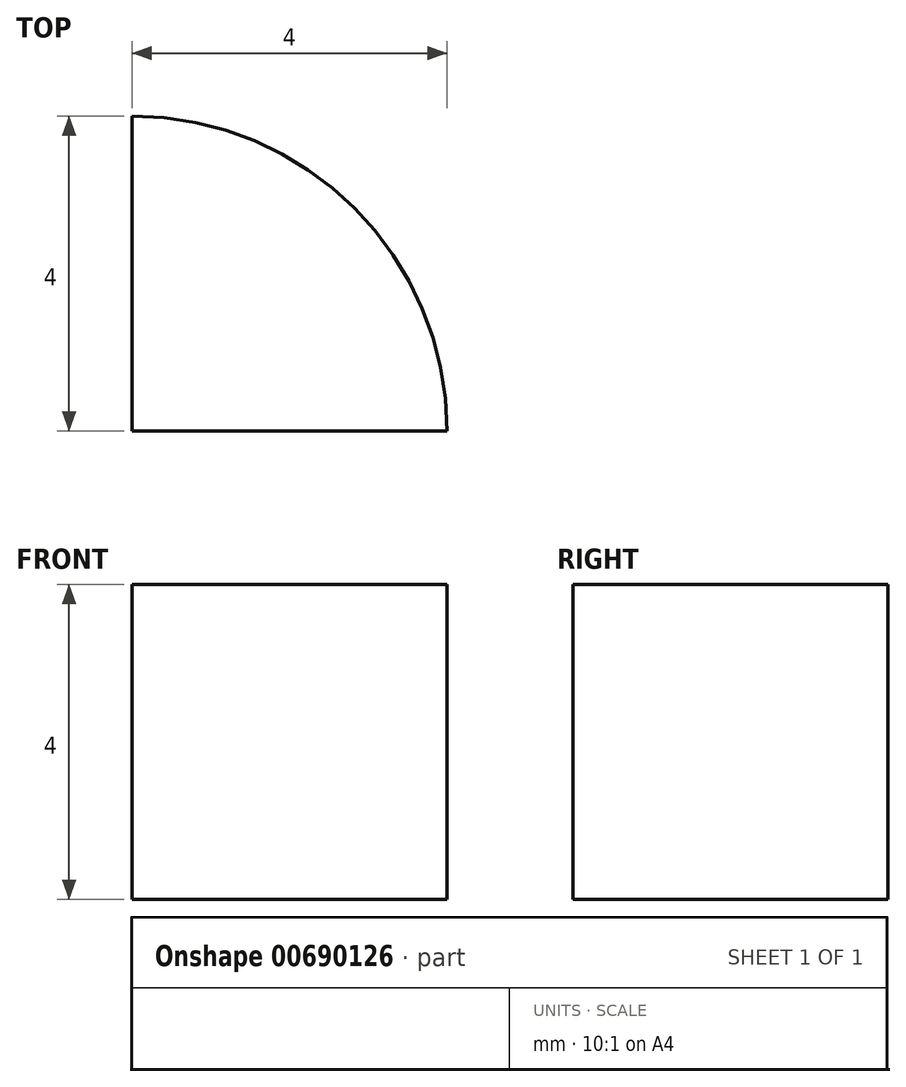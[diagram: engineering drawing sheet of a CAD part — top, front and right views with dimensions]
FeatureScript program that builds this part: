
annotation { "Feature Type Name" : "Feature", "Feature Type Description" : "" }
export const myFeature = defineFeature(function(context is Context, id is Id, definition is map)
    precondition{}
    {
        {
            var Q0;
            Q0=qCreatedBy(makeId("Right.planeOp"),FACE);
            var sketch = newSketch(context, id + "F0", { "sketchPlane" : qUnion([Q0])});
            skLineSegment(sketch, "E0.bottom", {"start": v(-1.53, 1.78) * mm, "end": v(2.47, 1.78) * mm});
            skLineSegment(sketch, "E0.top", {"start": v(-1.53, -2.22) * mm, "end": v(2.47, -2.22) * mm});
            skLineSegment(sketch, "E0.left", {"start": v(-1.53, 1.78) * mm, "end": v(-1.53, -2.22) * mm});
            skLineSegment(sketch, "E0.right", {"start": v(2.47, 1.78) * mm, "end": v(2.47, -2.22) * mm});
            skSolve(sketch);
        }
        {
            var Q0;
            Q0=makeQuery(id+"F0.imprint","IMPRINT",FACE,{"disambiguationData":[TD([[makeQuery(id+"F0.imprint","IMPRINT",EDGE,{"derivedFrom":sQuery(id+"F0.wireOp",EDGE,"E0.bottom")}),-1.0]])]});
            var Q1;
            Q1=sQuery(id+"F0.wireOp",EDGE,"E0.left");
            revolve(context, id + "F1", {"entities" : qUnion([Q0]), "axis" : qUnion([Q1]), "revolveType" : RevolveType.ONE_DIRECTION, "angle" : 90 * degree});
        }
    });
